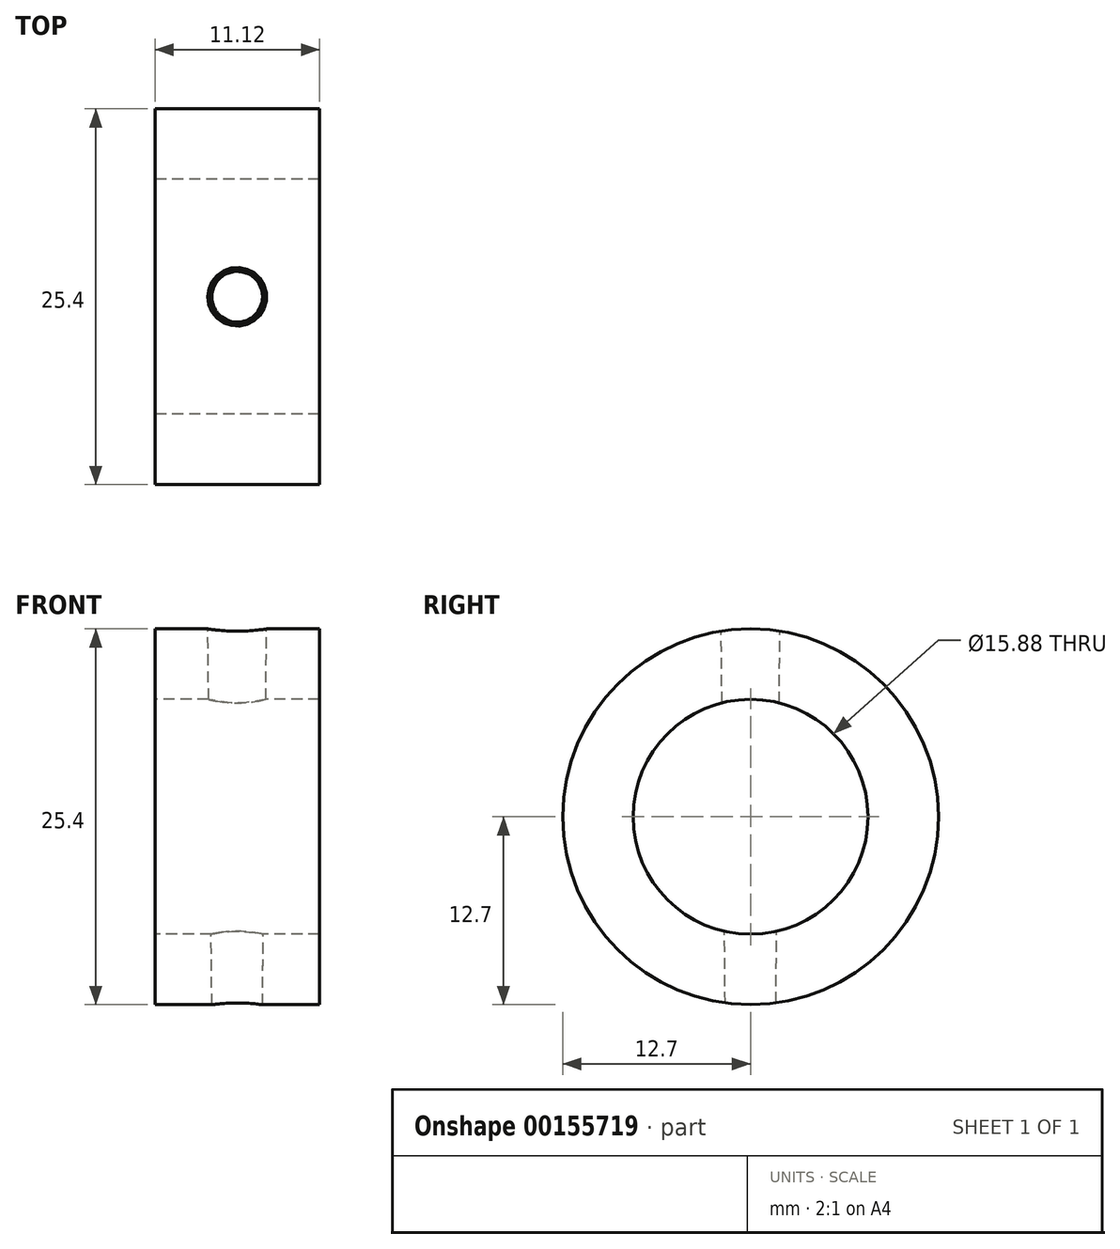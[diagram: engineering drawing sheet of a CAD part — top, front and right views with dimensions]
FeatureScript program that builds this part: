
annotation { "Feature Type Name" : "Feature", "Feature Type Description" : "" }
export const myFeature = defineFeature(function(context is Context, id is Id, definition is map)
    precondition{}
    {
        {
            var Q0;
            Q0=qCreatedBy(makeId("Right.planeOp"),FACE);
            var sketch = newSketch(context, id + "F2", { "sketchPlane" : qUnion([Q0])});
            skCircle(sketch, "E0", {"center": v(0, 0) * mm, "radius": 7.94 * mm});
            skCircle(sketch, "E1", {"center": v(0, 0) * mm, "radius": 12.7 * mm});
            skSolve(sketch);
        }
        {
            var Q0;
            Q0 = qSketchRegion(id + "F2", true);
            extrude(context, id + "F0", {"entities" : qUnion([Q0]), "endBound" : BoundingType.SYMMETRIC, "depth" : 11.1 * mm});
        }
        {
            var Q0;
            Q0=qCreatedBy(makeId("Front.planeOp"),FACE);
            var sketch = newSketch(context, id + "F1", { "sketchPlane" : qUnion([Q0])});
            skLineSegment(sketch, "E2", {"start": v(1.98, 12.28) * mm, "end": v(1.71, -12.39) * mm});
            skLineSegment(sketch, "E3", {"start": v(0, 12.7) * mm, "end": v(0, -12.7) * mm});
            skArc(sketch, "E4", {"start": v(1.98, 12.28) * mm, "mid": v(1.01, 12.6) * mm, "end": v(0, 12.7) * mm, "construction": true});
            skArc(sketch, "E5", {"start": v(0, -12.7) * mm, "mid": v(0.87, -12.62) * mm, "end": v(1.71, -12.39) * mm, "construction": true});
            skLineSegment(sketch, "E6", {"start": v(1.98, 12.28) * mm, "end": v(1.99, 12.7) * mm});
            skLineSegment(sketch, "E7", {"start": v(1.99, 12.7) * mm, "end": v(0, 12.7) * mm});
            skLineSegment(sketch, "E8", {"start": v(1.71, -12.39) * mm, "end": v(1.71, -12.7) * mm});
            skLineSegment(sketch, "E9", {"start": v(1.71, -12.7) * mm, "end": v(0, -12.7) * mm});
            skSolve(sketch);
        }
        {
            var Q0;
            Q0 = qSketchRegion(id + "F1", true);
            var Q1;
            Q1=sQuery(id+"F1.wireOp",EDGE,"E3");
            revolve(context, id + "F3", {"operationType" : NewBodyOperationType.REMOVE, "entities" : qUnion([Q0]), "axis" : qUnion([Q1]), "revolveType" : RevolveType.FULL, "oppositeDirection" : true});
        }
    });
